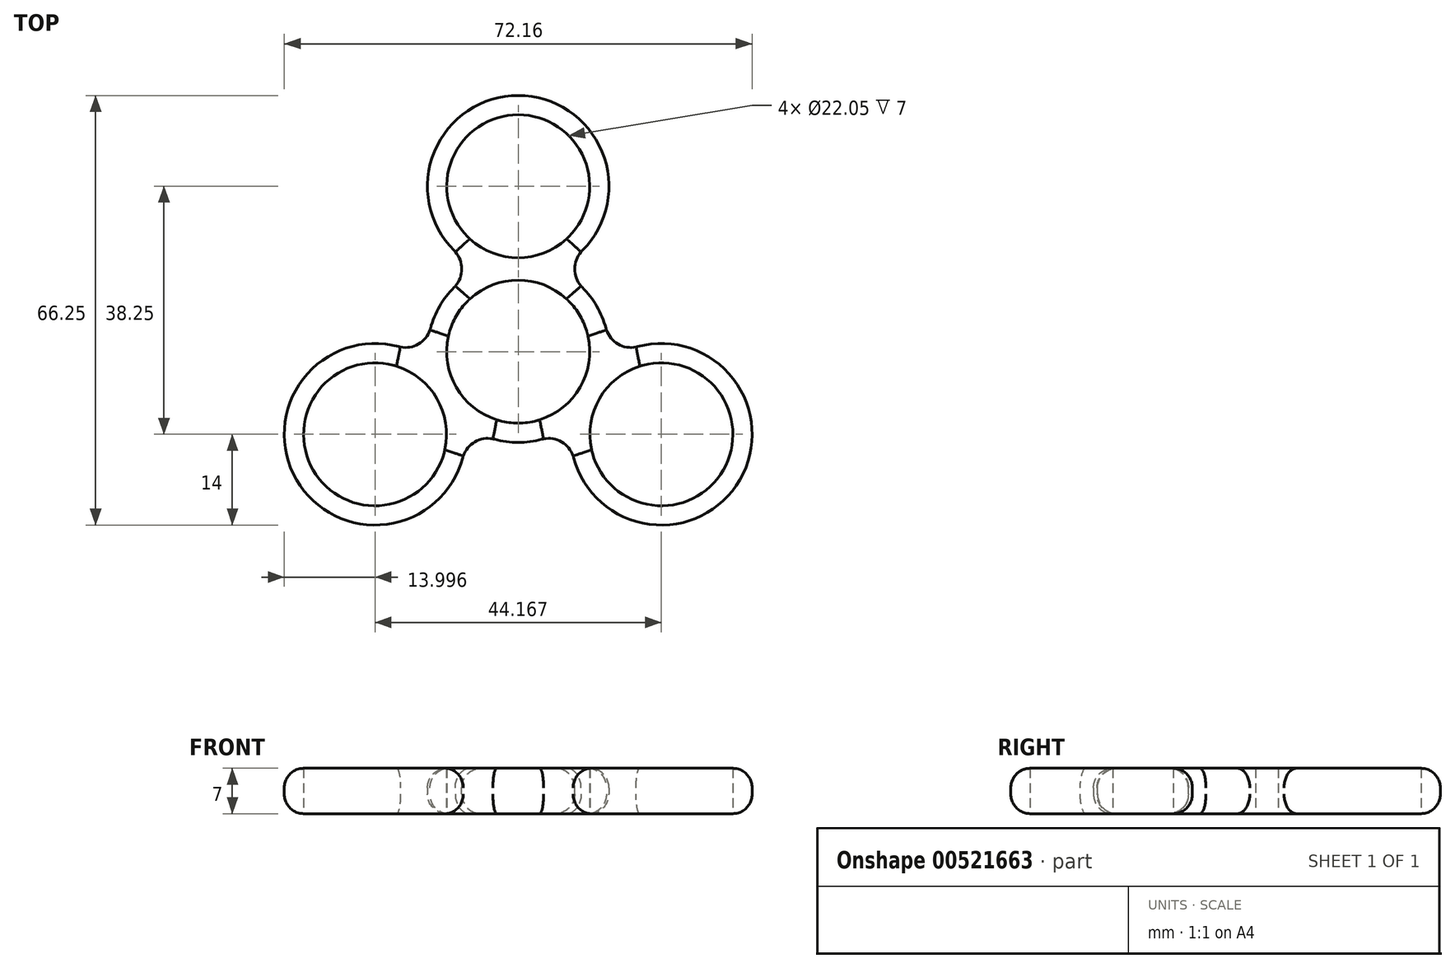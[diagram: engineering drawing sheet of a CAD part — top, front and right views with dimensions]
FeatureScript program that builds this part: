
annotation { "Feature Type Name" : "Feature", "Feature Type Description" : "" }
export const myFeature = defineFeature(function(context is Context, id is Id, definition is map)
    precondition{}
    {
        {
            var Q0;
            Q0=qCreatedBy(makeId("Top.planeOp"),FACE);
            var sketch = newSketch(context, id + "F0", { "sketchPlane" : qUnion([Q0])});
            skCircle(sketch, "E0", {"center": v(0, 25.5) * mm, "radius": 11.03 * mm});
            skCircle(sketch, "E1.1.0", {"center": v(-22.08, -12.75) * mm, "radius": 11.03 * mm});
            skCircle(sketch, "E1.2.0", {"center": v(22.08, -12.75) * mm, "radius": 11.03 * mm});
            skPoint(sketch, "E1.center", {"position": v(0, 0) * mm});
            skCircle(sketch, "E2", {"center": v(0, 25.5) * mm, "radius": 14 * mm});
            skCircle(sketch, "E3.1.0", {"center": v(-22.08, -12.75) * mm, "radius": 14 * mm});
            skCircle(sketch, "E3.2.0", {"center": v(22.08, -12.75) * mm, "radius": 14 * mm});
            skCircle(sketch, "E4", {"center": v(0, 0) * mm, "radius": 11.03 * mm});
            skCircle(sketch, "E5", {"center": v(0, 0) * mm, "radius": 14 * mm});
            skSolve(sketch);
        }
        {
            var Q0;
            Q0=makeQuery(id+"F0.imprint","IMPRINT",FACE,{"disambiguationData":[TD([[makeQuery(id+"F0.imprint","IMPRINT",EDGE,{"derivedFrom":sQuery(id+"F0.wireOp",EDGE,"E1.2.0")}),-1.0]])]});
            var Q1;
            {var subQ0=sQuery(id+"F0.wireOp",EDGE,"E5");var subQ1=sQuery(id+"F0.wireOp",EDGE,"E3.2.0");var subQ2=makeQuery(id+"F0.imprint","INTERSECT",VERTEX,{"disambiguationData":[OD(0.0)],"derivedFrom":[subQ1,subQ0]});Q1=makeQuery(id+"F0.imprint","IMPRINT",FACE,{"disambiguationData":[TD([[makeQuery(id+"F0.imprint","IMPRINT",EDGE,{"disambiguationData":[TD([[subQ2,1.0]])],"derivedFrom":subQ1}),1.0]])]});}
            var Q2;
            Q2=makeQuery(id+"F0.imprint","IMPRINT",FACE,{"disambiguationData":[TD([[makeQuery(id+"F0.imprint","IMPRINT",EDGE,{"derivedFrom":sQuery(id+"F0.wireOp",EDGE,"E4")}),-1.0]])]});
            var Q3;
            {var subQ0=sQuery(id+"F0.wireOp",EDGE,"E5");var subQ1=sQuery(id+"F0.wireOp",EDGE,"E3.1.0");var subQ2=makeQuery(id+"F0.imprint","INTERSECT",VERTEX,{"disambiguationData":[OD(0.0)],"derivedFrom":[subQ1,subQ0]});Q3=makeQuery(id+"F0.imprint","IMPRINT",FACE,{"disambiguationData":[TD([[makeQuery(id+"F0.imprint","IMPRINT",EDGE,{"disambiguationData":[TD([[subQ2,1.0]])],"derivedFrom":subQ1}),1.0]])]});}
            var Q4;
            {var subQ0=sQuery(id+"F0.wireOp",EDGE,"E5");var subQ1=sQuery(id+"F0.wireOp",EDGE,"E2");var subQ2=makeQuery(id+"F0.imprint","INTERSECT",VERTEX,{"disambiguationData":[OD(0.0)],"derivedFrom":[subQ1,subQ0]});Q4=makeQuery(id+"F0.imprint","IMPRINT",FACE,{"disambiguationData":[TD([[makeQuery(id+"F0.imprint","IMPRINT",EDGE,{"disambiguationData":[TD([[subQ2,-1.0]])],"derivedFrom":subQ1}),1.0]])]});}
            var Q5;
            Q5=makeQuery(id+"F0.imprint","IMPRINT",FACE,{"disambiguationData":[TD([[makeQuery(id+"F0.imprint","IMPRINT",EDGE,{"derivedFrom":sQuery(id+"F0.wireOp",EDGE,"E0")}),-1.0]])]});
            var Q6;
            Q6=makeQuery(id+"F0.imprint","IMPRINT",FACE,{"disambiguationData":[TD([[makeQuery(id+"F0.imprint","IMPRINT",EDGE,{"derivedFrom":sQuery(id+"F0.wireOp",EDGE,"E1.1.0")}),-1.0]])]});
            extrude(context, id + "F1", {"entities" : qUnion([Q0, Q1, Q2, Q3, Q4, Q5, Q6]), "depth" : 7 * mm, "offsetDistance" : 25 * mm});
        }
        {
            var Q0;
            {var subQ0=sQuery(id+"F0.wireOp",EDGE,"E5");var subQ1=sQuery(id+"F0.wireOp",EDGE,"E3.1.0");Q0=makeQuery(id+"F1.opExtrude","SWEPT_EDGE",EDGE,{"disambiguationData":[OSD([subQ1,subQ0]),TDD([makeQuery(id+"F0.imprint","INTERSECT",VERTEX,{"disambiguationData":[OD(0.0)],"derivedFrom":[subQ1,subQ0]})])]});}
            var Q1;
            {var subQ0=sQuery(id+"F0.wireOp",EDGE,"E5");var subQ1=sQuery(id+"F0.wireOp",EDGE,"E2");Q1=makeQuery(id+"F1.opExtrude","SWEPT_EDGE",EDGE,{"disambiguationData":[OSD([subQ1,subQ0]),TDD([makeQuery(id+"F0.imprint","INTERSECT",VERTEX,{"disambiguationData":[OD(0.0)],"derivedFrom":[subQ1,subQ0]})])]});}
            var Q2;
            {var subQ0=sQuery(id+"F0.wireOp",EDGE,"E5");var subQ1=sQuery(id+"F0.wireOp",EDGE,"E3.1.0");Q2=makeQuery(id+"F1.opExtrude","SWEPT_EDGE",EDGE,{"disambiguationData":[OSD([subQ1,subQ0]),TDD([makeQuery(id+"F0.imprint","INTERSECT",VERTEX,{"disambiguationData":[OD(1.0)],"derivedFrom":[subQ1,subQ0]})])]});}
            var Q3;
            {var subQ0=sQuery(id+"F0.wireOp",EDGE,"E5");var subQ1=sQuery(id+"F0.wireOp",EDGE,"E3.2.0");Q3=makeQuery(id+"F1.opExtrude","SWEPT_EDGE",EDGE,{"disambiguationData":[OSD([subQ1,subQ0]),TDD([makeQuery(id+"F0.imprint","INTERSECT",VERTEX,{"disambiguationData":[OD(0.0)],"derivedFrom":[subQ1,subQ0]})])]});}
            var Q4;
            {var subQ0=sQuery(id+"F0.wireOp",EDGE,"E5");var subQ1=sQuery(id+"F0.wireOp",EDGE,"E3.2.0");Q4=makeQuery(id+"F1.opExtrude","SWEPT_EDGE",EDGE,{"disambiguationData":[OSD([subQ1,subQ0]),TDD([makeQuery(id+"F0.imprint","INTERSECT",VERTEX,{"disambiguationData":[OD(1.0)],"derivedFrom":[subQ1,subQ0]})])]});}
            var Q5;
            {var subQ0=sQuery(id+"F0.wireOp",EDGE,"E5");var subQ1=sQuery(id+"F0.wireOp",EDGE,"E2");Q5=makeQuery(id+"F1.opExtrude","SWEPT_EDGE",EDGE,{"disambiguationData":[OSD([subQ1,subQ0]),TDD([makeQuery(id+"F0.imprint","INTERSECT",VERTEX,{"disambiguationData":[OD(1.0)],"derivedFrom":[subQ1,subQ0]})])]});}
            fillet(context, id + "F2", {"entities" : qUnion([Q0, Q1, Q2, Q3, Q4, Q5]), "radius" : 4 * mm, "tangentPropagation" : true, "allowEdgeOverflow" : false});
        }
        {
            var Q0;
            Q0=makeQuery(id+"F1.opExtrude","CAP_EDGE",EDGE,{"disambiguationData":[OSD([sQuery(id+"F0.wireOp",EDGE,"E3.1.0")])],"isStart":false});
            var Q1;
            Q1=makeQuery(id+"F1.opExtrude","CAP_EDGE",EDGE,{"disambiguationData":[OSD([sQuery(id+"F0.wireOp",EDGE,"E3.1.0")])],"isStart":true});
            fillet(context, id + "F3", {"entities" : qUnion([Q0, Q1]), "radius" : 3 * mm, "tangentPropagation" : true, "allowEdgeOverflow" : false});
        }
    });
